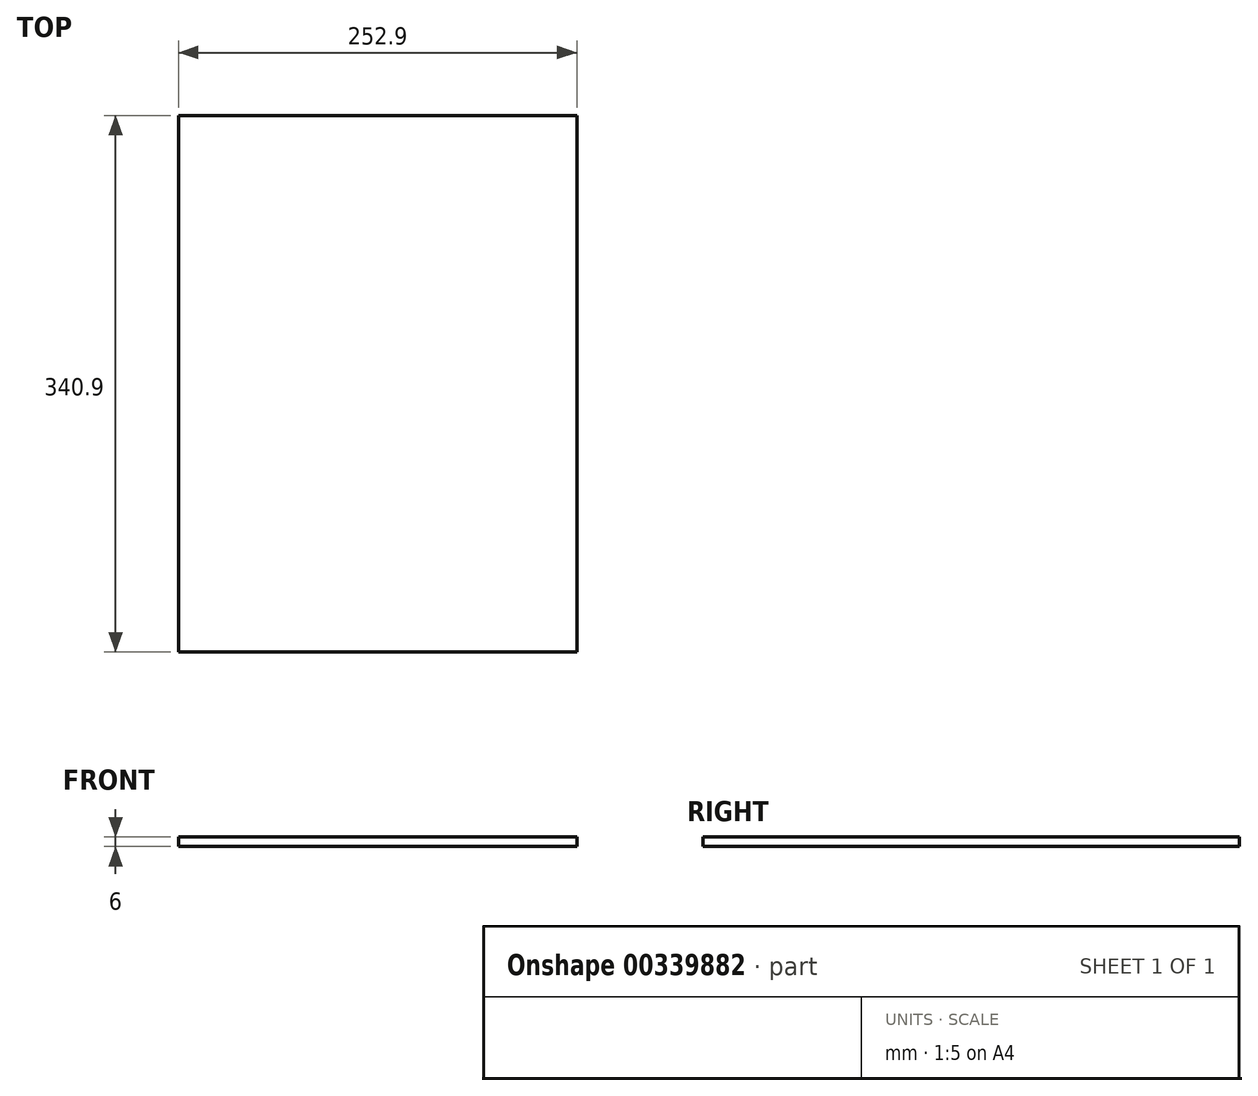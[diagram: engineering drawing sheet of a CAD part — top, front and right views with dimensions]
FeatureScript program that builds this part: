
annotation { "Feature Type Name" : "Feature", "Feature Type Description" : "" }
export const myFeature = defineFeature(function(context is Context, id is Id, definition is map)
    precondition{}
    {
        {
            var Q0;
            Q0=qCreatedBy(makeId("Top.planeOp"),FACE);
            var sketch = newSketch(context, id + "F0", { "sketchPlane" : qUnion([Q0])});
            skLineSegment(sketch, "E0.bottom", {"start": v(-205.09, 295.63) * mm, "end": v(47.81, 295.63) * mm});
            skLineSegment(sketch, "E0.top", {"start": v(-205.09, -45.27) * mm, "end": v(47.81, -45.27) * mm});
            skLineSegment(sketch, "E0.left", {"start": v(-205.09, 295.63) * mm, "end": v(-205.09, -45.27) * mm});
            skLineSegment(sketch, "E0.right", {"start": v(47.81, 295.63) * mm, "end": v(47.81, -45.27) * mm});
            skSolve(sketch);
        }
        {
            var Q0;
            Q0 = qSketchRegion(id + "F0", true);
            extrude(context, id + "F1", {"entities" : qUnion([Q0]), "depth" : 6 * mm, "offsetDistance" : 25 * mm});
        }
    });
